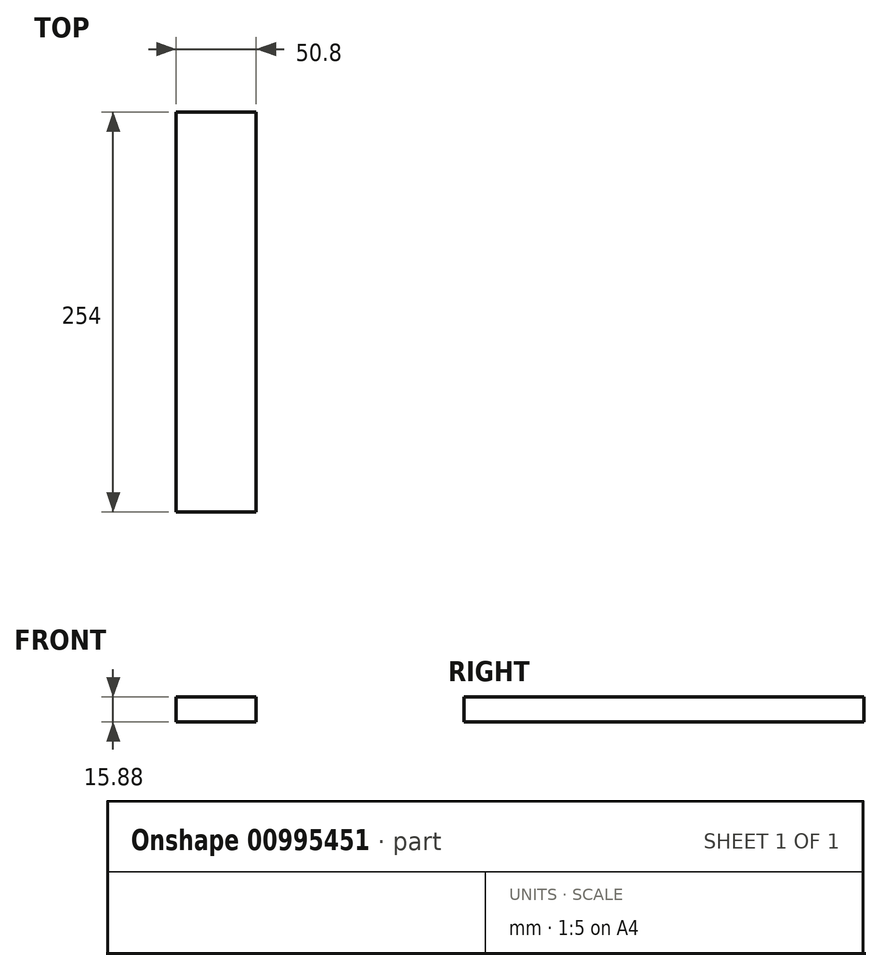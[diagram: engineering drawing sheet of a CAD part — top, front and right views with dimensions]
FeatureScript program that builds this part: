
annotation { "Feature Type Name" : "Feature", "Feature Type Description" : "" }
export const myFeature = defineFeature(function(context is Context, id is Id, definition is map)
    precondition{}
    {
        {
            var Q0;
            Q0=qCreatedBy(makeId("Front.planeOp"),FACE);
            var sketch = newSketch(context, id + "F0", { "sketchPlane" : qUnion([Q0])});
            skLineSegment(sketch, "E0.bottom", {"start": v(0, 0) * mm, "end": v(50.8, 0) * mm});
            skLineSegment(sketch, "E0.top", {"start": v(0, 15.87) * mm, "end": v(50.8, 15.87) * mm});
            skLineSegment(sketch, "E0.left", {"start": v(0, 0) * mm, "end": v(0, 15.87) * mm});
            skLineSegment(sketch, "E0.right", {"start": v(50.8, 0) * mm, "end": v(50.8, 15.87) * mm});
            skSolve(sketch);
        }
        {
            var Q0;
            Q0=makeQuery(id+"F0.imprint","IMPRINT",FACE,{"disambiguationData":[TD([[makeQuery(id+"F0.imprint","IMPRINT",EDGE,{"derivedFrom":sQuery(id+"F0.wireOp",EDGE,"E0.bottom")}),1.0]])]});
            extrude(context, id + "F1", {"entities" : qUnion([Q0]), "oppositeDirection" : true, "depth" : 254 * mm, "offsetDistance" : 25.4 * mm});
        }
    });
